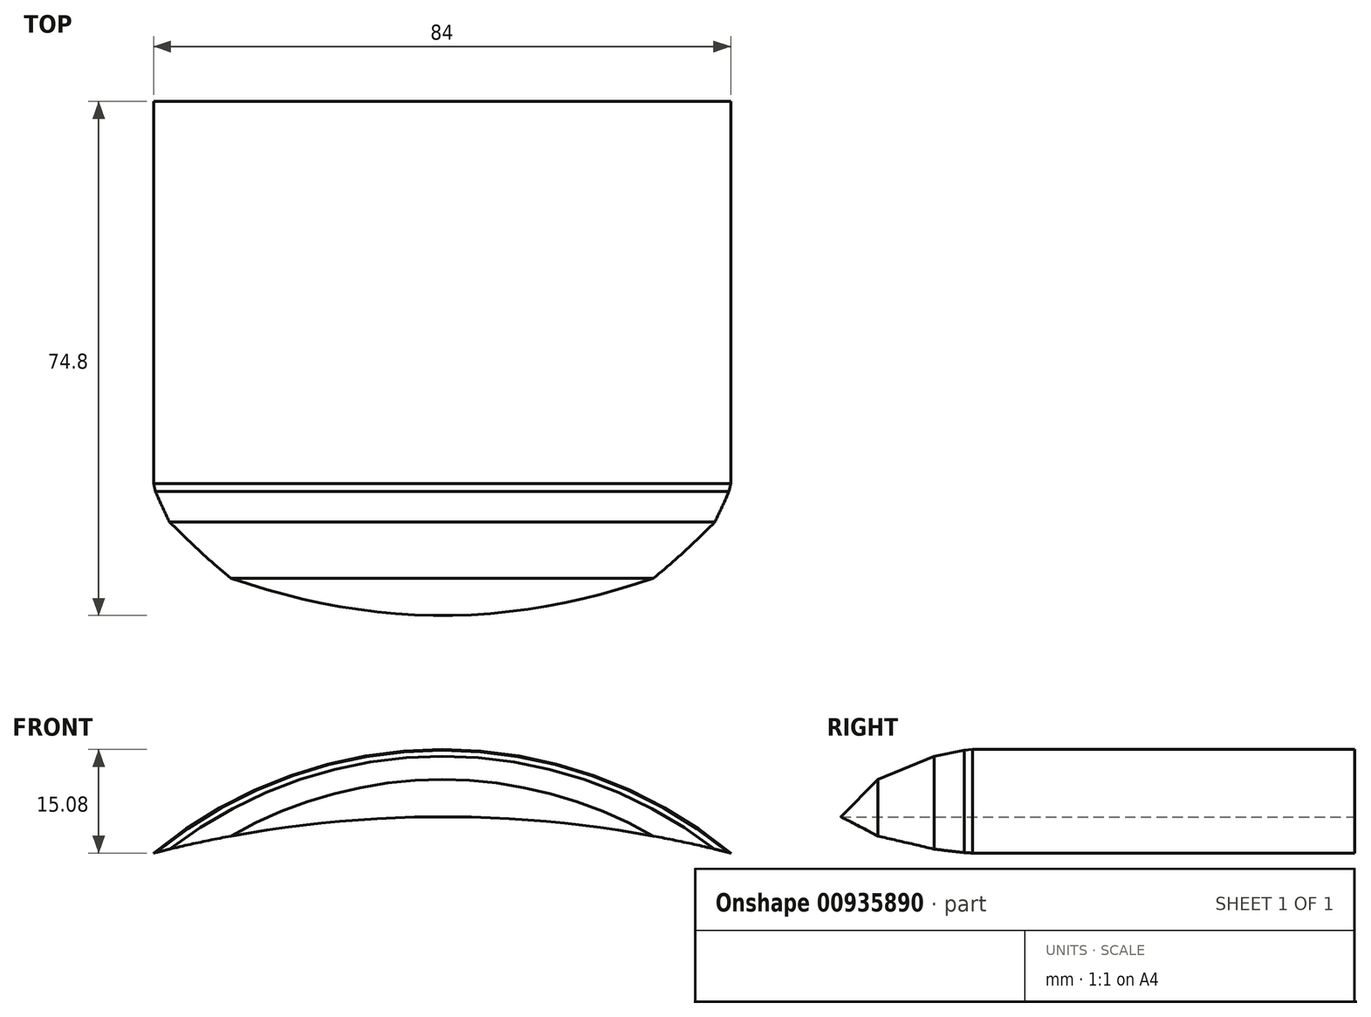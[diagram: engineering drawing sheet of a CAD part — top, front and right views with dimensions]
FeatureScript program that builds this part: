
annotation { "Feature Type Name" : "Feature", "Feature Type Description" : "" }
export const myFeature = defineFeature(function(context is Context, id is Id, definition is map)
    precondition{}
    {
        {
            var Q0;
            Q0=qCreatedBy(makeId("Front.planeOp"),FACE);
            var sketch = newSketch(context, id + "F0", { "sketchPlane" : qUnion([Q0])});
            skPoint(sketch, "E0.start.orphan", {"position": v(0, 7.94) * mm});
            skLineSegment(sketch, "E1", {"start": v(0, 7.94) * mm, "end": v(0, 2.94) * mm});
            skLineSegment(sketch, "E2", {"start": v(0, 2.94) * mm, "end": v(42, 2.94) * mm});
            skLineSegment(sketch, "E3", {"start": v(0, 2.94) * mm, "end": v(-42, 2.94) * mm});
            skArc(sketch, "E4", {"start": v(42, 2.94) * mm, "mid": v(0, 8.22) * mm, "end": v(-42, 2.94) * mm});
            skLineSegment(sketch, "E5", {"start": v(0, 7.94) * mm, "end": v(0, 18.02) * mm});
            skArc(sketch, "E6", {"start": v(42, 2.94) * mm, "mid": v(0, 18.02) * mm, "end": v(-42, 2.94) * mm});
            skSolve(sketch);
        }
        {
            var Q0;
            {var subQ0=sQuery(id+"F0.wireOp",EDGE,"E6");var subQ3=sQuery(id+"F0.wireOp",EDGE,"E5");var subQ5=makeQuery(id+"F0.imprint","INTERSECT",VERTEX,{"derivedFrom":[subQ3,subQ0]});Q0=makeQuery(id+"F0.imprint","IMPRINT",FACE,{"disambiguationData":[TD([[makeQuery(id+"F0.imprint","IMPRINT",EDGE,{"disambiguationData":[TD([[subQ5,1.0]])],"derivedFrom":subQ3}),-1.0]])]});}
            var Q1;
            {var subQ0=sQuery(id+"F0.wireOp",EDGE,"E6");var subQ3=sQuery(id+"F0.wireOp",EDGE,"E5");var subQ5=makeQuery(id+"F0.imprint","INTERSECT",VERTEX,{"derivedFrom":[subQ3,subQ0]});Q1=makeQuery(id+"F0.imprint","IMPRINT",FACE,{"disambiguationData":[TD([[makeQuery(id+"F0.imprint","IMPRINT",EDGE,{"disambiguationData":[TD([[subQ5,1.0]])],"derivedFrom":subQ3}),1.0]])]});}
            extrude(context, id + "F1", {"entities" : qUnion([Q0, Q1]), "depth" : 75 * mm, "offsetDistance" : 25 * mm});
        }
        {
            var Q0;
            Q0=makeQuery(id+"F1.opExtrude","CAP_EDGE",EDGE,{"disambiguationData":[OSD([sQuery(id+"F0.wireOp",EDGE,"E6")])],"isStart":false});
            chamfer(context, id + "F2", {"entities" : qUnion([Q0]), "width" : 10 * mm, "tangentPropagation" : true});
        }
        {
            var Q0;
            {var subQ0=sQuery(id+"F0.wireOp",EDGE,"E6");Q0=makeQuery(id+"F2.opChamfer","BLEND_EDGE",EDGE,{"blendedFrom":[makeQuery(id+"F1.opExtrude","CAP_EDGE",EDGE,{"disambiguationData":[OSD([subQ0])],"isStart":false}),makeQuery(id+"F1.opExtrude","SWEPT_FACE",FACE,{"disambiguationData":[OSD([subQ0])]})],"blendedInto":[makeQuery(id+"F1.opExtrude","SWEPT_FACE",FACE,{"disambiguationData":[OSD([subQ0])]})]});}
            chamfer(context, id + "F3", {"entities" : qUnion([Q0]), "width" : 15 * mm, "tangentPropagation" : true});
        }
        {
            var Q0;
            {var subQ0=sQuery(id+"F0.wireOp",EDGE,"E6");var subQ1=makeQuery(id+"F1.opExtrude","SWEPT_FACE",FACE,{"disambiguationData":[OSD([subQ0])]});Q0=makeQuery(id+"F3.opChamfer","BLEND_EDGE",EDGE,{"blendedFrom":[makeQuery(id+"F2.opChamfer","BLEND_EDGE",EDGE,{"blendedFrom":[makeQuery(id+"F1.opExtrude","CAP_EDGE",EDGE,{"disambiguationData":[OSD([subQ0])],"isStart":false}),subQ1],"blendedInto":[subQ1]}),subQ1],"blendedInto":[subQ1]});}
            chamfer(context, id + "F4", {"entities" : qUnion([Q0]), "width" : 13 * mm, "tangentPropagation" : true});
        }
        {
            var Q0;
            {var subQ0=sQuery(id+"F0.wireOp",EDGE,"E6");var subQ1=makeQuery(id+"F1.opExtrude","SWEPT_FACE",FACE,{"disambiguationData":[OSD([subQ0])]});var subQ2=subQ1;Q0=makeQuery(id+"F4.opChamfer","BLEND_EDGE",EDGE,{"blendedFrom":[makeQuery(id+"F3.opChamfer","BLEND_EDGE",EDGE,{"blendedFrom":[makeQuery(id+"F2.opChamfer","BLEND_EDGE",EDGE,{"blendedFrom":[makeQuery(id+"F1.opExtrude","CAP_EDGE",EDGE,{"disambiguationData":[OSD([subQ0])],"isStart":false}),subQ1],"blendedInto":[subQ1]}),subQ2],"blendedInto":[subQ2]}),subQ2],"blendedInto":[subQ2]});}
            chamfer(context, id + "F5", {"entities" : qUnion([Q0]), "width" : 6 * mm, "tangentPropagation" : true});
        }
    });
